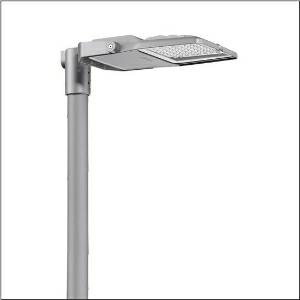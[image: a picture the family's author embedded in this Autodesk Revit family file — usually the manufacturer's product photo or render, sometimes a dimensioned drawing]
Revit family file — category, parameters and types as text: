
# Revit family: floodlight_fl_21_iq_mini___pl61_5xa7772d2c3a_9c70
name_source: partatom
category: Lighting Fixtures
units: mm (PartAtom-declared; Revit-internal decimal feet)

## family parameters
Cut with Voids When Loaded = No
Host = Face
Light Source = No
Part Type = Normal
Room Calculation Point = No
Round Connector Dimension = Use Diameter
Shared = No

## types (1)
- --- (1 x LED, 17500 lm, 143 W, 3000K)
    Apparent Load = 143 VA
    CIE Flux Codes = 33 65 98 100 100
    Color Rendering = 70
    Color Temperature = 3000K
    Default Elevation = 1800 mm
    Description = Floodlight FL 21 iQ mini, floodlight, primary light control with lens, of PMMA, primary optical cover: protective disc, of toughened safety glass, transparent, light distribution: PL61, light emission: direct distribution, installation type: surface-mounted, LED, High Power LED, rated luminous flux: 17.500lm, luminous efficacy: 122lm/W, light colour: 730, colour temperature: 3000K, control gear: iQ Street-Remote/DALI, control: Auto-Match, Temp-Guard, Night-Set, Smart-Wire, Desk-Remote (wireless, voltage-free reading and setting of iQ features in the workshop via application-optimized NFC function/RFID function), optimised constant luminous flux control (CLO 2.0), Light-Fading, Lumen-Switch, with terminal, 6-pole, mains connection: 220..240V, AC, 50/60Hz, start of lifetime: 143W, end of service life: 152W, reduction: 61W, luminaire housing, of diecast aluminium, powder-coated, Siteco® metallic grey (DB 702S), corrosivity category C5 mid according to DIN EN ISO 12944, suitable for swimming pools, chlorine-resistant, sealing non-destructively replaceable, please order mast flange separately, mast bracket, of steel, galvanised, powder-coated, protection rating (complete): IP66, insulation class (complete): insulation class II (safety insulation), certification: CE, ENEC, VDE, protection symbol: D, impact resistance: IK08, permissible operating ambient temperature: -40..+40°C, permissible operating ambient temperature for outdoor applications: -40..+50°C, standard: DIN EN 12944, LABS conformity tested according to VDMA 24364:2018-05, packaging unit: 1 piece

Light Distribution: PL61
    Height = 70 mm
    Lamp = 1 x LED
    Lamp Light Flux = 17500 lm
    Lamp Power = 143 W
    Lamp count = 1
    Length = 485 mm
    Luminous efficacy = 122 lm/W
    Manufacturer = Siteco
    ModVariant = No
    Model = 5XA7772D2C3A
    Number of Poles = 1
    OnlyDefault = Yes
    Power Factor = 1
    Product Name = Floodlight FL 21 iQ mini | PL61
    Product group = floodlight | pylon annexe
    ProductGroupID = 6200
    Protection Class = Protection class II
    Protection Degree = IP 66
    RLX_Detail_Level = 1
    RLX_Emergency_Light_Flux = 0 lm
    RLX_Emergency_Type = 0
    RLX_Emergency_Type_DB = No
    RlxData = <blob elided: 101785 chars, md5=94af37ae>
    Socket = socket
    Standby Power = 0 W
    System Light Flux = 17500 lm
    System Power = 143 W
    Type Comments = factory setting: luminous flux: 100 % | dim-lin: 254 | 730 mA
    Type Image = l_1007125.jpg
    URL = http://relux.com
    VarID = @adj_172452
    Voltage = 0 V
    Weight = 0.00 kg
    Width = 337 mm

## geometry (parser evidence)
native form markers: Blend x4, Sweep x11
no freeform markers — native parametric forms only
